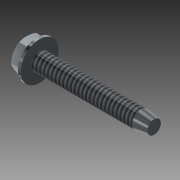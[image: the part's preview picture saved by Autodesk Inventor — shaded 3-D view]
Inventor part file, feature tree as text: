
AUTODESK INVENTOR PART (.ipt)
format: ipt  version: 2018 (Build 220112000, 112)  size: 189,952 bytes
history: native  units: mm (DEFAULTED — no unit token found)
features: sketch x4, extrude x2, other x1, chamfer x1, plane x1
ambient origin geometry x8: Origin, YZ Plane, XZ Plane, XY Plane, X Axis, Y Axis, Z Axis, Center Point
bodies: Solid1 (feature_tree), Body (feature_tree)
feature tree (9):
  extrude  "Head"  Depth=0.7874mm
  other  "IDS_WORKPLANE{1}"
  extrude  "Indent"  TaperAngle=90.0deg  [1 undecoded]
  chamfer  "Chamfer1"  [1 undecoded]
  plane  "Work Plane3"
  sketch  "Sketch1"  dims[d1=0.7874mm d2=4.826mm]
  sketch  "Sketch2"  dims[d3=31.75mm d77=90.0deg]
  sketch  "Sketch3"  dims[d6=31.75mm]
  sketch  "Sketch4"  dims[d7=0.0mm d10=0.0mm d11=7.9248mm d12=3.048mm d13=0.0mm d14=0.0mm d15=6.33984mm d16=0.3048mm d17=0.0mm d92=90.0deg d19=0.5334mm d20=3.7084mm d21=7.9248mm d22=10.5156mm d23=6.863078mm d98=45.0deg d99=0.0mm d100=0.0mm]
note: 2 required parameter values undecoded (feature->parameter linkage not recoverable at this tier; creation-order binding heuristic only, values carry confidence <= 0.55)
